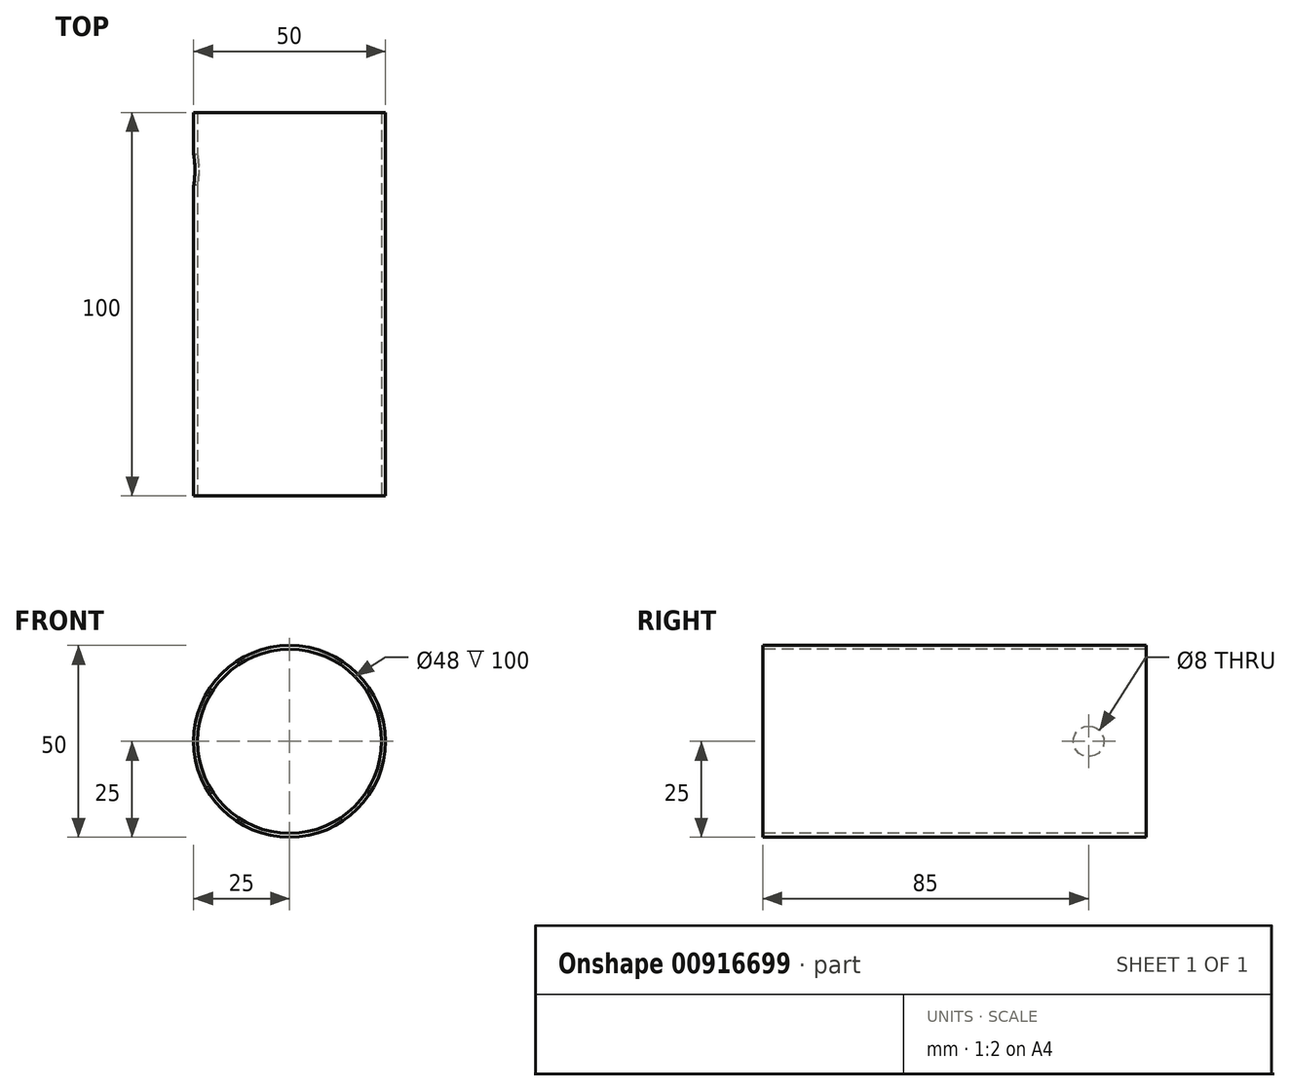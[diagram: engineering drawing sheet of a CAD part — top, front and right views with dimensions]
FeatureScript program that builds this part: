
annotation { "Feature Type Name" : "Feature", "Feature Type Description" : "" }
export const myFeature = defineFeature(function(context is Context, id is Id, definition is map)
    precondition{}
    {
        {
            var Q0;
            Q0=qCreatedBy(makeId("Front.planeOp"),FACE);
            var sketch = newSketch(context, id + "F0", { "sketchPlane" : qUnion([Q0])});
            skCircle(sketch, "E0", {"center": v(0, 0) * mm, "radius": 25 * mm});
            skCircle(sketch, "E1", {"center": v(0, 0) * mm, "radius": 24 * mm});
            skSolve(sketch);
        }
        {
            var Q0;
            Q0=qCreatedBy(makeId("Right.planeOp"),FACE);
            var sketch = newSketch(context, id + "F1", { "sketchPlane" : qUnion([Q0])});
            skLineSegment(sketch, "E2", {"start": v(0, 0) * mm, "end": v(-100, 0) * mm});
            skSolve(sketch);
        }
        {
            var Q0;
            Q0 = qSketchRegion(id + "F0", true);
            var Q1;
            Q1 = qConstructionFilter(qBodyType(qCreatedBy(id + "F1" ,EDGE), BodyType.WIRE), ConstructionObject.NO);
            sweep(context, id + "F2", {"profiles" : qUnion([Q0]), "path" : qUnion([Q1])});
        }
        {
            var Q0;
            Q0=qCreatedBy(makeId("Right.planeOp"),FACE);
            var sketch = newSketch(context, id + "F3", { "sketchPlane" : qUnion([Q0])});
            skCircle(sketch, "E3", {"center": v(-15, 0) * mm, "radius": 4 * mm});
            skSolve(sketch);
        }
        {
            var Q0;
            Q0=qCreatedBy(makeId("Top.planeOp"),FACE);
            var sketch = newSketch(context, id + "F4", { "sketchPlane" : qUnion([Q0])});
            skLineSegment(sketch, "E4", {"start": v(0, -15) * mm, "end": v(-40, -15) * mm});
            skSolve(sketch);
        }
        {
            var Q0;
            Q0 = qSketchRegion(id + "F3", true);
            var Q1;
            Q1=sQuery(id+"F3.wireOp",EDGE,"E3");
            var Q2;
            Q2 = qConstructionFilter(qBodyType(qCreatedBy(id + "F4" ,EDGE), BodyType.WIRE), ConstructionObject.NO);
            sweep(context, id + "F5", {"operationType" : NewBodyOperationType.REMOVE, "profiles" : qUnion([Q0]), "surfaceProfiles" : qUnion([Q1]), "path" : qUnion([Q2])});
        }
    });
